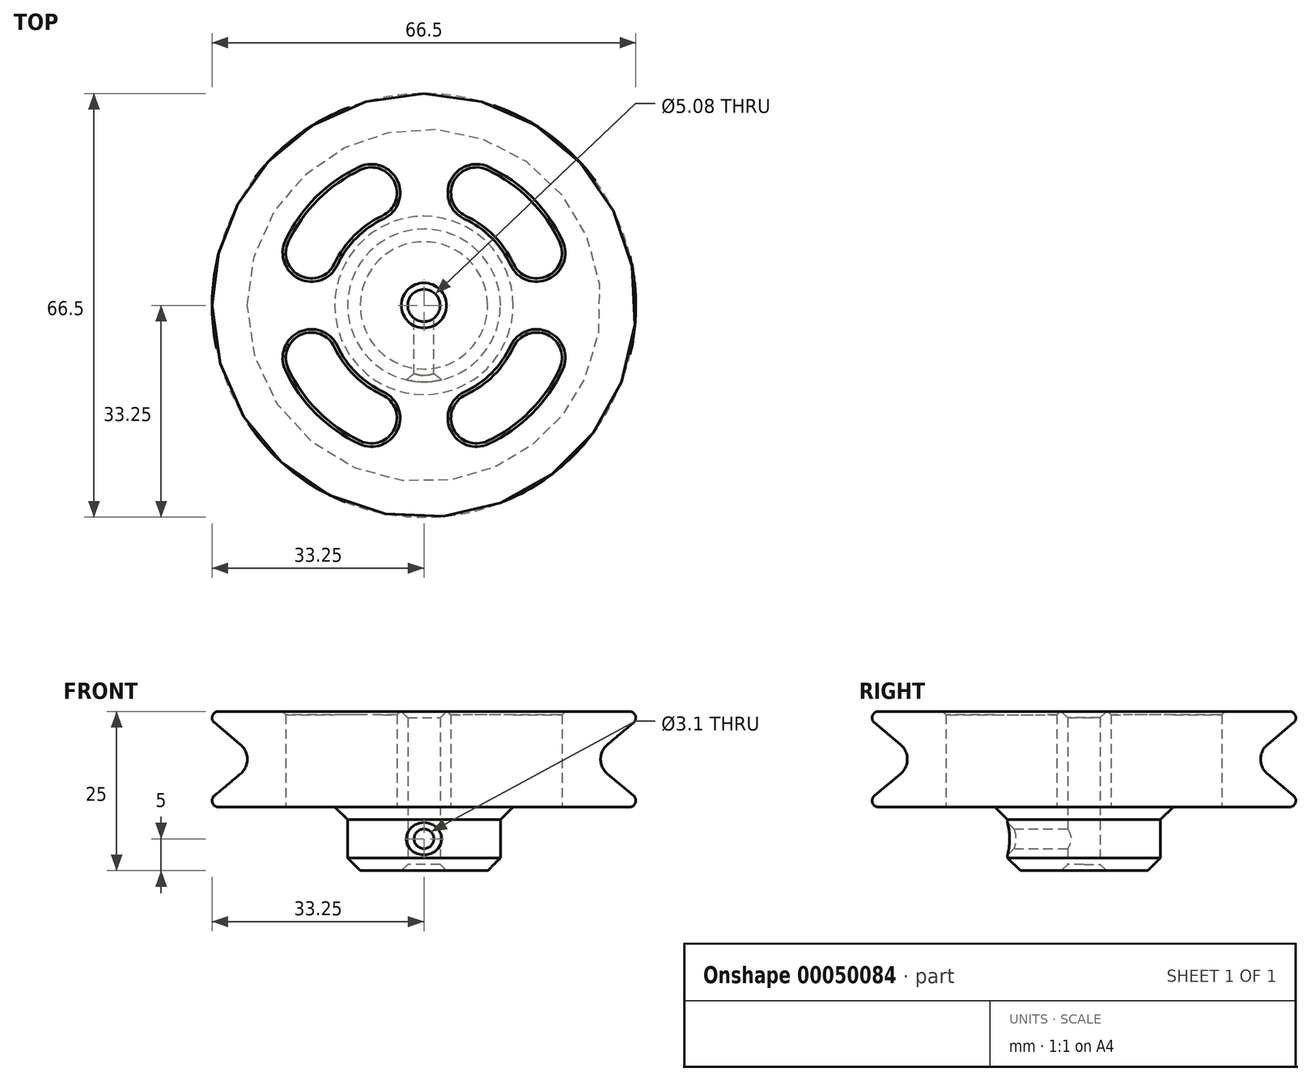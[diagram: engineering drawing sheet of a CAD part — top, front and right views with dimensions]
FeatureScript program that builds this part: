
annotation { "Feature Type Name" : "Feature", "Feature Type Description" : "" }
export const myFeature = defineFeature(function(context is Context, id is Id, definition is map)
    precondition{}
    {
        {
            var Q0;
            Q0=qCreatedBy(makeId("Front.planeOp"),FACE);
            var sketch = newSketch(context, id + "F0", { "sketchPlane" : qUnion([Q0])});
            skLineSegment(sketch, "E0", {"start": v(2.54, 25) * mm, "end": v(35, 25) * mm});
            skLineSegment(sketch, "E1", {"start": v(35, 25) * mm, "end": v(26.06, 17.5) * mm});
            skLineSegment(sketch, "E2", {"start": v(26.06, 17.5) * mm, "end": v(35, 10) * mm});
            skLineSegment(sketch, "E3", {"start": v(35, 10) * mm, "end": v(12, 10) * mm});
            skLineSegment(sketch, "E4", {"start": v(12, 10) * mm, "end": v(12, 0) * mm});
            skLineSegment(sketch, "E5", {"start": v(12, 0) * mm, "end": v(2.54, 0) * mm});
            skLineSegment(sketch, "E6", {"start": v(2.54, 25) * mm, "end": v(2.54, 0) * mm});
            skPoint(sketch, "E7.orphan", {"position": v(0, 25) * mm});
            skPoint(sketch, "E8.orphan", {"position": v(0, 0) * mm});
            skLineSegment(sketch, "E9", {"start": v(0, 0) * mm, "end": v(0, 35.33) * mm, "construction": true});
            skSolve(sketch);
        }
        {
            var Q0;
            Q0 = qSketchRegion(id + "F0", true);
            var Q1;
            Q1=sQuery(id+"F0.wireOp",EDGE,"E9");
            revolve(context, id + "F1", {"entities" : qUnion([Q0]), "axis" : qUnion([Q1]), "revolveType" : RevolveType.FULL});
        }
        {
            var Q0;
            Q0=makeQuery(id+"F1.opRevolve","SWEPT_EDGE",EDGE,{"disambiguationData":[OSD([sQuery(id+"F0.wireOp",EDGE,"E4"),sQuery(id+"F0.wireOp",EDGE,"E5")])]});
            chamfer(context, id + "F2", {"entities" : qUnion([Q0]), "width" : 2 * mm, "tangentPropagation" : true});
        }
        {
            var Q0;
            Q0=makeQuery(id+"F1.opRevolve","SWEPT_EDGE",EDGE,{"disambiguationData":[OSD([sQuery(id+"F0.wireOp",EDGE,"E5"),sQuery(id+"F0.wireOp",EDGE,"E6")])]});
            var Q1;
            Q1=makeQuery(id+"F1.opRevolve","SWEPT_EDGE",EDGE,{"disambiguationData":[OSD([sQuery(id+"F0.wireOp",EDGE,"E0"),sQuery(id+"F0.wireOp",EDGE,"E6")])]});
            chamfer(context, id + "F3", {"entities" : qUnion([Q0, Q1]), "width" : 1 * mm, "tangentPropagation" : true});
        }
        {
            var Q0;
            Q0=makeQuery(id+"F1.opRevolve","SWEPT_EDGE",EDGE,{"disambiguationData":[OSD([sQuery(id+"F0.wireOp",EDGE,"E3"),sQuery(id+"F0.wireOp",EDGE,"E4")])]});
            chamfer(context, id + "F4", {"entities" : qUnion([Q0]), "width" : 2 * mm, "tangentPropagation" : true});
        }
        {
            var Q0;
            Q0=makeQuery(id+"F1.opRevolve","SWEPT_EDGE",EDGE,{"disambiguationData":[OSD([sQuery(id+"F0.wireOp",EDGE,"E1"),sQuery(id+"F0.wireOp",EDGE,"E2")])]});
            fillet(context, id + "F5", {"entities" : qUnion([Q0]), "radius" : 3 * mm, "tangentPropagation" : true, "allowEdgeOverflow" : false});
        }
        {
            var Q0;
            Q0=makeQuery(id+"F1.opRevolve","SWEPT_EDGE",EDGE,{"disambiguationData":[OSD([sQuery(id+"F0.wireOp",EDGE,"E2"),sQuery(id+"F0.wireOp",EDGE,"E3")])]});
            var Q1;
            Q1=makeQuery(id+"F1.opRevolve","SWEPT_EDGE",EDGE,{"disambiguationData":[OSD([sQuery(id+"F0.wireOp",EDGE,"E0"),sQuery(id+"F0.wireOp",EDGE,"E1")])]});
            fillet(context, id + "F6", {"entities" : qUnion([Q0, Q1]), "radius" : 1 * mm, "tangentPropagation" : true, "allowEdgeOverflow" : false});
        }
        {
            var Q0;
            Q0=makeQuery(id+"F1.opRevolve","SWEPT_FACE",FACE,{"disambiguationData":[OSD([sQuery(id+"F0.wireOp",EDGE,"E3")])]});
            var sketch = newSketch(context, id + "F7", { "sketchPlane" : qUnion([Q0])});
            skLineSegment(sketch, "E10", {"start": v(0, 0) * mm, "end": v(-16.81, 36.06) * mm, "construction": true});
            skLineSegment(sketch, "E11", {"start": v(0, 0) * mm, "end": v(-41.38, 19.3) * mm, "construction": true});
            skArc(sketch, "E12", {"start": v(-6.55, 14.05) * mm, "mid": v(-4.62, 19.36) * mm, "end": v(-9.93, 21.3) * mm});
            skArc(sketch, "E13", {"start": v(-6.55, 14.05) * mm, "mid": v(-10.96, 10.96) * mm, "end": v(-14.05, 6.55) * mm});
            skArc(sketch, "E14", {"start": v(-9.93, 21.3) * mm, "mid": v(-16.62, 16.62) * mm, "end": v(-21.3, 9.93) * mm});
            skArc(sketch, "E15", {"start": v(-21.3, 9.93) * mm, "mid": v(-19.36, 4.62) * mm, "end": v(-14.05, 6.55) * mm});
            skArc(sketch, "E16.MirrorCS", {"start": v(21.3, 9.93) * mm, "mid": v(19.36, 4.62) * mm, "end": v(14.05, 6.55) * mm});
            skArc(sketch, "E17.MirrorCS", {"start": v(9.93, 21.3) * mm, "mid": v(16.62, 16.62) * mm, "end": v(21.3, 9.93) * mm});
            skArc(sketch, "E18.MirrorCS", {"start": v(6.55, 14.05) * mm, "mid": v(4.62, 19.36) * mm, "end": v(9.93, 21.3) * mm});
            skArc(sketch, "E19.MirrorCS", {"start": v(6.55, 14.05) * mm, "mid": v(10.96, 10.96) * mm, "end": v(14.05, 6.55) * mm});
            skArc(sketch, "E20.MirrorCS", {"start": v(21.3, -9.93) * mm, "mid": v(19.36, -4.62) * mm, "end": v(14.05, -6.55) * mm});
            skArc(sketch, "E21.MirrorCS", {"start": v(9.93, -21.3) * mm, "mid": v(16.62, -16.62) * mm, "end": v(21.3, -9.93) * mm});
            skArc(sketch, "E22.MirrorCS", {"start": v(6.55, -14.05) * mm, "mid": v(10.96, -10.96) * mm, "end": v(14.05, -6.55) * mm});
            skArc(sketch, "E23.MirrorCS", {"start": v(6.55, -14.05) * mm, "mid": v(4.62, -19.36) * mm, "end": v(9.93, -21.3) * mm});
            skArc(sketch, "E24.MirrorCS", {"start": v(-21.3, -9.93) * mm, "mid": v(-19.36, -4.62) * mm, "end": v(-14.05, -6.55) * mm});
            skArc(sketch, "E25.MirrorCS", {"start": v(-6.55, -14.05) * mm, "mid": v(-4.62, -19.36) * mm, "end": v(-9.93, -21.3) * mm});
            skArc(sketch, "E26.MirrorCS", {"start": v(-9.93, -21.3) * mm, "mid": v(-16.62, -16.62) * mm, "end": v(-21.3, -9.93) * mm});
            skArc(sketch, "E27.MirrorCS", {"start": v(-6.55, -14.05) * mm, "mid": v(-10.96, -10.96) * mm, "end": v(-14.05, -6.55) * mm});
            skSolve(sketch);
        }
        {
            var Q0;
            Q0 = qSketchRegion(id + "F7", true);
            extrude(context, id + "F8", {"entities" : qUnion([Q0]), "operationType" : NewBodyOperationType.REMOVE, "endBound" : BoundingType.THROUGH_ALL, "oppositeDirection" : true, "depth" : 25 * mm});
        }
        {
            var Q0;
            Q0=qCreatedBy(makeId("Front.planeOp"),FACE);
            var sketch = newSketch(context, id + "F9", { "sketchPlane" : qUnion([Q0])});
            skCircle(sketch, "E28", {"center": v(0, 5) * mm, "radius": 1.55 * mm});
            skSolve(sketch);
        }
        {
            var Q0;
            Q0 = qSketchRegion(id + "F9", true);
            extrude(context, id + "F10", {"entities" : qUnion([Q0]), "operationType" : NewBodyOperationType.REMOVE, "endBound" : BoundingType.THROUGH_ALL, "depth" : 25 * mm});
        }
        {
            var Q0;
            Q0=makeQuery(id+"F10.boolean.opBoolean","INTERSECT",EDGE,{"derivedFrom":[makeQuery(id+"F1.opRevolve","SWEPT_FACE",FACE,{"disambiguationData":[OSD([sQuery(id+"F0.wireOp",EDGE,"E4")])]}),makeQuery(id+"F10.opExtrude","SWEPT_FACE",FACE,{"disambiguationData":[OSD([sQuery(id+"F9.wireOp",EDGE,"E28")])]})]});
            chamfer(context, id + "F11", {"entities" : qUnion([Q0]), "width" : 1 * mm, "tangentPropagation" : true});
        }
        {
            var Q0;
            Q0=makeQuery(id+"F8.boolean.opBoolean","INTERSECT",EDGE,{"derivedFrom":[makeQuery(id+"F1.opRevolve","SWEPT_FACE",FACE,{"disambiguationData":[OSD([sQuery(id+"F0.wireOp",EDGE,"E0")])]}),makeQuery(id+"F8.opExtrude","SWEPT_FACE",FACE,{"disambiguationData":[OSD([sQuery(id+"F7.wireOp",EDGE,"E13")])]})]});
            var Q1;
            Q1=makeQuery(id+"F8.boolean.opBoolean","INTERSECT",EDGE,{"derivedFrom":[makeQuery(id+"F1.opRevolve","SWEPT_FACE",FACE,{"disambiguationData":[OSD([sQuery(id+"F0.wireOp",EDGE,"E0")])]}),makeQuery(id+"F8.opExtrude","SWEPT_FACE",FACE,{"disambiguationData":[OSD([sQuery(id+"F7.wireOp",EDGE,"E27.MirrorCS")])]})]});
            var Q2;
            Q2=makeQuery(id+"F8.boolean.opBoolean","INTERSECT",EDGE,{"derivedFrom":[makeQuery(id+"F1.opRevolve","SWEPT_FACE",FACE,{"disambiguationData":[OSD([sQuery(id+"F0.wireOp",EDGE,"E0")])]}),makeQuery(id+"F8.opExtrude","SWEPT_FACE",FACE,{"disambiguationData":[OSD([sQuery(id+"F7.wireOp",EDGE,"E22.MirrorCS")])]})]});
            var Q3;
            Q3=makeQuery(id+"F8.boolean.opBoolean","INTERSECT",EDGE,{"derivedFrom":[makeQuery(id+"F1.opRevolve","SWEPT_FACE",FACE,{"disambiguationData":[OSD([sQuery(id+"F0.wireOp",EDGE,"E0")])]}),makeQuery(id+"F8.opExtrude","SWEPT_FACE",FACE,{"disambiguationData":[OSD([sQuery(id+"F7.wireOp",EDGE,"E19.MirrorCS")])]})]});
            var Q4;
            Q4=makeQuery(id+"F8.boolean.opBoolean","COPY",EDGE,{"derivedFrom":makeQuery(id+"F8.opExtrude","CAP_EDGE",EDGE,{"disambiguationData":[OSD([sQuery(id+"F7.wireOp",EDGE,"E21.MirrorCS")])],"isStart":true})});
            var Q5;
            Q5=makeQuery(id+"F8.boolean.opBoolean","COPY",EDGE,{"derivedFrom":makeQuery(id+"F8.opExtrude","CAP_EDGE",EDGE,{"disambiguationData":[OSD([sQuery(id+"F7.wireOp",EDGE,"E17.MirrorCS")])],"isStart":true})});
            var Q6;
            Q6=makeQuery(id+"F8.boolean.opBoolean","COPY",EDGE,{"derivedFrom":makeQuery(id+"F8.opExtrude","CAP_EDGE",EDGE,{"disambiguationData":[OSD([sQuery(id+"F7.wireOp",EDGE,"E13")])],"isStart":true})});
            var Q7;
            Q7=makeQuery(id+"F8.boolean.opBoolean","COPY",EDGE,{"derivedFrom":makeQuery(id+"F8.opExtrude","CAP_EDGE",EDGE,{"disambiguationData":[OSD([sQuery(id+"F7.wireOp",EDGE,"E27.MirrorCS")])],"isStart":true})});
            chamfer(context, id + "F12", {"entities" : qUnion([Q0, Q1, Q2, Q3, Q4, Q5, Q6, Q7]), "width" : .5 * mm, "tangentPropagation" : true});
        }
    });
